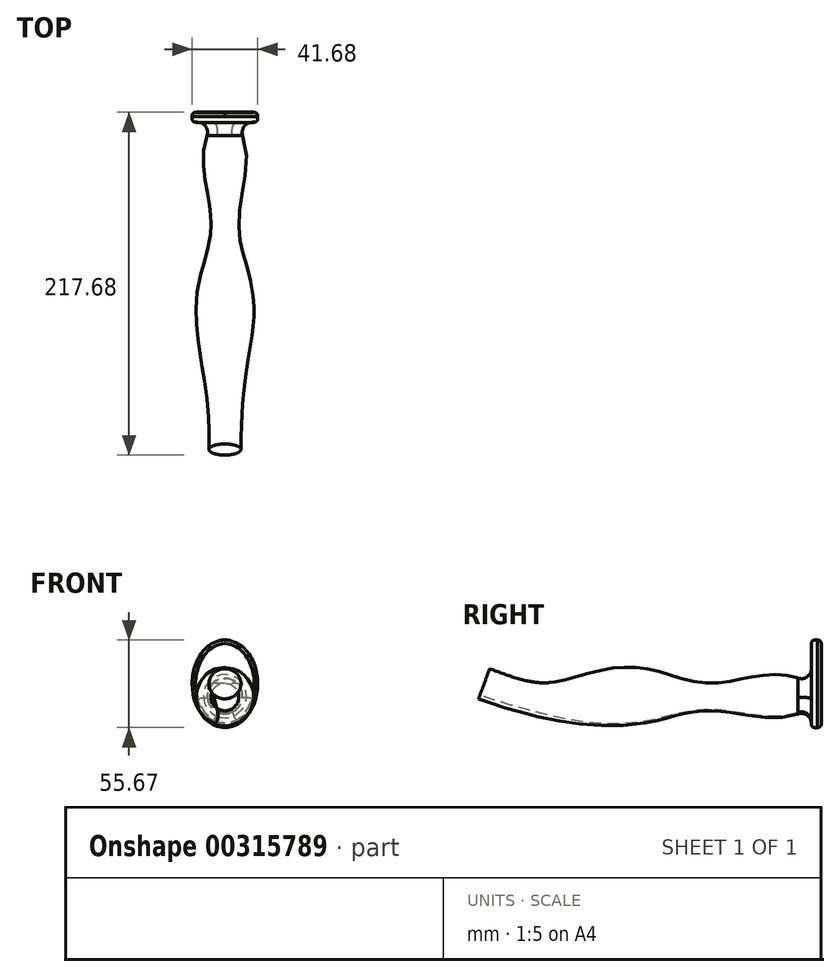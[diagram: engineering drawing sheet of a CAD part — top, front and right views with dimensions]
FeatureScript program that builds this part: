
annotation { "Feature Type Name" : "Feature", "Feature Type Description" : "" }
export const myFeature = defineFeature(function(context is Context, id is Id, definition is map)
    precondition{}
    {
        {
            var Q0;
            Q0=qCreatedBy(makeId("Right.planeOp"),FACE);
            var sketch = newSketch(context, id + "F0", { "sketchPlane" : qUnion([Q0])});
            skFitSpline(sketch, "E0", {"points": [v(115.17, 0) * mm, v(98.93, 0) * mm, v(43.84, 0) * mm, v(-16.91, 0) * mm, v(-57.65, -2.17) * mm, v(-73.7, 0.2) * mm, v(-95.84, 8) * mm, v(-97.86, 10.3) * mm], "startDerivative": vector(-162.4, -0.08) * mm, "endDerivative": vector(-93.3, 133.3) * mm});
            skSolve(sketch);
        }
        {
            var Q0;
            Q0=sQuery(id+"F0.wireOp",VERTEX,"E0.start");
            var Q1;
            Q1=sQuery(id+"F0.wireOp",EDGE,"E0");
            cPlane(context, id + "F1", {"entities" : qUnion([Q0, Q1]), "cplaneType" : CPlaneType.CURVE_POINT, "offset" : 25.4 * mm, "width" : 152.4 * mm, "height" : 152.4 * mm});
        }
        {
            var Q0;
            Q0=sQuery(id+"F0.wireOp",VERTEX,"E0.1.internal");
            var Q1;
            Q1=sQuery(id+"F0.wireOp",EDGE,"E0");
            cPlane(context, id + "F2", {"entities" : qUnion([Q0, Q1]), "cplaneType" : CPlaneType.CURVE_POINT, "offset" : 25.4 * mm, "width" : 152.4 * mm, "height" : 152.4 * mm});
        }
        {
            var Q0;
            Q0=sQuery(id+"F0.wireOp",VERTEX,"E0.2.internal");
            var Q1;
            Q1=sQuery(id+"F0.wireOp",EDGE,"E0");
            cPlane(context, id + "F3", {"entities" : qUnion([Q0, Q1]), "cplaneType" : CPlaneType.CURVE_POINT, "offset" : 25.4 * mm, "width" : 152.4 * mm, "height" : 152.4 * mm});
        }
        {
            var Q0;
            Q0=sQuery(id+"F0.wireOp",EDGE,"E0");
            cPoint(context, id + "F4", {"entities" : qUnion([Q0]), "parameter" : 0.5});
        }
        {
            var Q0;
            Q0 = qCreatedBy(id + "F4" ,VERTEX);
            var Q1;
            Q1=sQuery(id+"F0.wireOp",EDGE,"E0");
            cPlane(context, id + "F5", {"entities" : qUnion([Q0, Q1]), "cplaneType" : CPlaneType.CURVE_POINT, "offset" : 25.4 * mm, "width" : 152.4 * mm, "height" : 152.4 * mm});
        }
        {
            var Q0;
            Q0=sQuery(id+"F0.wireOp",VERTEX,"E0.3.internal");
            var Q1;
            Q1=sQuery(id+"F0.wireOp",EDGE,"E0");
            cPlane(context, id + "F6", {"entities" : qUnion([Q0, Q1]), "cplaneType" : CPlaneType.CURVE_POINT, "offset" : 25.4 * mm, "width" : 152.4 * mm, "height" : 152.4 * mm});
        }
        {
            var Q0;
            Q0=sQuery(id+"F0.wireOp",VERTEX,"E0.4.internal");
            var Q1;
            Q1=sQuery(id+"F0.wireOp",EDGE,"E0");
            cPlane(context, id + "F7", {"entities" : qUnion([Q0, Q1]), "cplaneType" : CPlaneType.CURVE_POINT, "offset" : 25.4 * mm, "width" : 152.4 * mm, "height" : 152.4 * mm});
        }
        {
            var Q0;
            Q0=sQuery(id+"F0.wireOp",VERTEX,"E0.6.internal");
            var Q1;
            Q1=sQuery(id+"F0.wireOp",EDGE,"E0");
            cPlane(context, id + "F8", {"entities" : qUnion([Q0, Q1]), "cplaneType" : CPlaneType.CURVE_POINT, "offset" : 25.4 * mm, "width" : 152.4 * mm, "height" : 152.4 * mm});
        }
        {
            var Q0;
            Q0=sQuery(id+"F0.wireOp",EDGE,"E0");
            var Q1;
            Q1=sQuery(id+"F0.wireOp",VERTEX,"E0.7.internal");
            cPlane(context, id + "F9", {"entities" : qUnion([Q0, Q1]), "cplaneType" : CPlaneType.CURVE_POINT, "offset" : 25.4 * mm, "width" : 152.4 * mm, "height" : 152.4 * mm});
        }
        {
            var Q0;
            Q0=qCreatedBy(id+"F1.planeOp",FACE);
            var sketch = newSketch(context, id + "F10", { "sketchPlane" : qUnion([Q0])});
            skCircle(sketch, "E1", {"center": v(0, 0) * mm, "radius": 6.35 * mm});
            skSolve(sketch);
        }
        {
            var Q0;
            Q0=qCreatedBy(id+"F2.planeOp",FACE);
            var sketch = newSketch(context, id + "F11", { "sketchPlane" : qUnion([Q0])});
            skCircle(sketch, "E2", {"center": v(0, 0) * mm, "radius": 12.7 * mm});
            skSolve(sketch);
        }
        {
            var Q0;
            Q0=qCreatedBy(id+"F3.planeOp",FACE);
            var sketch = newSketch(context, id + "F12", { "sketchPlane" : qUnion([Q0])});
            skCircle(sketch, "E3", {"center": v(0, 0) * mm, "radius": 8.9 * mm});
            skSolve(sketch);
        }
        {
            var Q0;
            Q0=qCreatedBy(id+"F5.planeOp",FACE);
            var sketch = newSketch(context, id + "F13", { "sketchPlane" : qUnion([Q0])});
            skCircle(sketch, "E4", {"center": v(0, 0.39) * mm, "radius": 17.15 * mm});
            skSolve(sketch);
        }
        {
            var Q0;
            Q0=qCreatedBy(id+"F6.planeOp",FACE);
            var sketch = newSketch(context, id + "F14", { "sketchPlane" : qUnion([Q0])});
            skCircle(sketch, "E5", {"center": v(0, 0) * mm, "radius": 18.03 * mm});
            skSolve(sketch);
        }
        {
            var Q0;
            Q0=qCreatedBy(id+"F7.planeOp",FACE);
            var sketch = newSketch(context, id + "F15", { "sketchPlane" : qUnion([Q0])});
            skCircle(sketch, "E6.cCircle", {"center": v(0, 0) * mm, "radius": 9.14 * mm, "construction": true});
            skLineSegment(sketch, "E6.0", {"start": v(-4.4, -10.67) * mm, "end": v(-11.44, 1.52) * mm});
            skLineSegment(sketch, "E6.1", {"start": v(-7.04, 9.14) * mm, "end": v(7.04, 9.14) * mm});
            skLineSegment(sketch, "E6.2", {"start": v(11.44, 1.52) * mm, "end": v(4.4, -10.67) * mm});
            skPoint(sketch, "E6.0.midPoint", {"position": v(-7.92, -4.57) * mm});
            skPoint(sketch, "E7.visualSharp", {"position": v(15.84, 9.14) * mm});
            skArc(sketch, "E7.filletArc", {"start": v(11.44, 1.52) * mm, "mid": v(11.44, 6.6) * mm, "end": v(7.04, 9.14) * mm});
            skPoint(sketch, "E8.visualSharp", {"position": v(-15.84, 9.14) * mm});
            skArc(sketch, "E8.filletArc", {"start": v(-7.04, 9.14) * mm, "mid": v(-11.44, 6.6) * mm, "end": v(-11.44, 1.52) * mm});
            skPoint(sketch, "E9.visualSharp", {"position": v(0, -18.29) * mm});
            skArc(sketch, "E9.filletArc", {"start": v(-4.4, -10.67) * mm, "mid": v(0, -13.2) * mm, "end": v(4.4, -10.67) * mm});
            skSolve(sketch);
        }
        {
            var Q0;
            Q0=qCreatedBy(id+"F9.planeOp",FACE);
            var sketch = newSketch(context, id + "F16", { "sketchPlane" : qUnion([Q0])});
            skLineSegment(sketch, "E10", {"start": v(12.2, -74.26) * mm, "end": v(-12.2, -74.26) * mm});
            skArc(sketch, "E11", {"start": v(12.2, -74.26) * mm, "mid": v(0, -62.06) * mm, "end": v(-12.2, -74.26) * mm});
            skSolve(sketch);
        }
        {
            var Q0;
            Q0=qCreatedBy(id+"F8.planeOp",FACE);
            var sketch = newSketch(context, id + "F17", { "sketchPlane" : qUnion([Q0])});
            skCircle(sketch, "E12", {"center": v(0, -25.45) * mm, "radius": 10.16 * mm});
            skSolve(sketch);
        }
        {
            var Q0;
            Q0=makeQuery(id+"F10.imprint","IMPRINT",FACE,{"disambiguationData":[TD([[makeQuery(id+"F10.imprint","IMPRINT",EDGE,{"derivedFrom":sQuery(id+"F10.wireOp",EDGE,"E1")}),1.0]])]});
            var Q1;
            Q1=makeQuery(id+"F11.imprint","IMPRINT",FACE,{"disambiguationData":[TD([[makeQuery(id+"F11.imprint","IMPRINT",EDGE,{"derivedFrom":sQuery(id+"F11.wireOp",EDGE,"E2")}),1.0]])]});
            var Q2;
            Q2=makeQuery(id+"F12.imprint","IMPRINT",FACE,{"disambiguationData":[TD([[makeQuery(id+"F12.imprint","IMPRINT",EDGE,{"derivedFrom":sQuery(id+"F12.wireOp",EDGE,"E3")}),1.0]])]});
            var Q3;
            Q3=makeQuery(id+"F13.imprint","IMPRINT",FACE,{"disambiguationData":[TD([[makeQuery(id+"F13.imprint","IMPRINT",EDGE,{"derivedFrom":sQuery(id+"F13.wireOp",EDGE,"E4")}),1.0]])]});
            var Q4;
            Q4=makeQuery(id+"F14.imprint","IMPRINT",FACE,{"disambiguationData":[TD([[makeQuery(id+"F14.imprint","IMPRINT",EDGE,{"derivedFrom":sQuery(id+"F14.wireOp",EDGE,"E5")}),1.0]])]});
            var Q5;
            Q5=makeQuery(id+"F15.imprint","IMPRINT",FACE,{"disambiguationData":[TD([[makeQuery(id+"F15.imprint","IMPRINT",EDGE,{"derivedFrom":sQuery(id+"F15.wireOp",EDGE,"E6.0")}),-1.0]])]});
            var Q6;
            Q6=makeQuery(id+"F17.imprint","IMPRINT",FACE,{"disambiguationData":[TD([[makeQuery(id+"F17.imprint","IMPRINT",EDGE,{"derivedFrom":sQuery(id+"F17.wireOp",EDGE,"E12")}),1.0]])]});
            loft(context, id + "F18", {"endCondition" : LoftEndDerivativeType.NORMAL_TO_PROFILE, "endMagnitude" : 1, "sheetProfilesArray" : [{ "sheetProfileEntities" : qUnion([Q0]) }, { "sheetProfileEntities" : qUnion([Q1]) }, { "sheetProfileEntities" : qUnion([Q2]) }, { "sheetProfileEntities" : qUnion([Q3]) }, { "sheetProfileEntities" : qUnion([Q4]) }, { "sheetProfileEntities" : qUnion([Q5]) }, { "sheetProfileEntities" : qUnion([Q6]) }]});
        }
        {
            var Q0;
            Q0=sQuery(id+"F16.wireOp",EDGE,"E11");
            var Q1;
            Q1=sQuery(id+"F16.wireOp",EDGE,"E10");
            revolve(context, id + "F19", {"bodyType" : ToolBodyType.SURFACE, "surfaceEntities" : qUnion([Q0]), "axis" : qUnion([Q1]), "revolveType" : RevolveType.FULL});
        }
        {
            var Q0;
            Q0=qCreatedBy(id+"F1.planeOp",FACE);
            var sketch = newSketch(context, id + "F20", { "sketchPlane" : qUnion([Q0])});
            skEllipse(sketch, "E13", {"center": v(0, 7.9) * mm, "majorRadius": 27.83 * mm, "minorRadius": 20.84 * mm, "majorAxis": v(0, 1)});
            skSolve(sketch);
        }
        {
            var Q0;
            Q0 = qSketchRegion(id + "F20", true);
            var Q1;
            Q1=makeQuery(id+"F20.imprint","IMPRINT",FACE,{"disambiguationData":[TD([[makeQuery(id+"F20.imprint","IMPRINT",EDGE,{"derivedFrom":sQuery(id+"F20.wireOp",EDGE,"E13")}),1.0]])]});
            extrude(context, id + "F21", {"entities" : qUnion([Q0, Q1]), "operationType" : NewBodyOperationType.ADD, "endBound" : BoundingType.SYMMETRIC, "depth" : 6.35 * mm});
        }
        {
            var Q0;
            Q0=makeQuery(id+"F21.opExtrude","CAP_EDGE",EDGE,{"disambiguationData":[OSD([sQuery(id+"F20.wireOp",EDGE,"E13")])],"isStart":false});
            fillet(context, id + "F22", {"entities" : qUnion([Q0]), "radius" : 2.3 * mm, "tangentPropagation" : true, "allowEdgeOverflow" : false});
        }
        {
            var Q0;
            Q0=makeQuery(id+"F21.boolean.opBoolean","INTERSECT",EDGE,{"derivedFrom":[makeQuery(id+"F18.opLoft","SWEPT_FACE",FACE,{"disambiguationData":[OSD([sQuery(id+"F10.wireOp",EDGE,"E1"),sQuery(id+"F11.wireOp",EDGE,"E2"),sQuery(id+"F15.wireOp",EDGE,"E6.0"),sQuery(id+"F15.wireOp",EDGE,"E9.filletArc")])]}),makeQuery(id+"F21.opExtrude","CAP_FACE",FACE,{"disambiguationData":[OSD([sQuery(id+"F20.wireOp",EDGE,"E13")])],"isStart":false})]});
            fillet(context, id + "F23", {"entities" : qUnion([Q0]), "radius" : 6.35 * mm, "tangentPropagation" : true, "allowEdgeOverflow" : false});
        }
        {
            var Q0;
            Q0=makeQuery(id+"F21.opExtrude","CAP_EDGE",EDGE,{"disambiguationData":[OSD([sQuery(id+"F20.wireOp",EDGE,"E13")])],"isStart":true});
            fillet(context, id + "F24", {"entities" : qUnion([Q0]), "radius" : 2.54 * mm, "tangentPropagation" : true, "rho" : 0.5, "crossSection" : FilletCrossSection.CONIC, "allowEdgeOverflow" : false});
        }
    });
